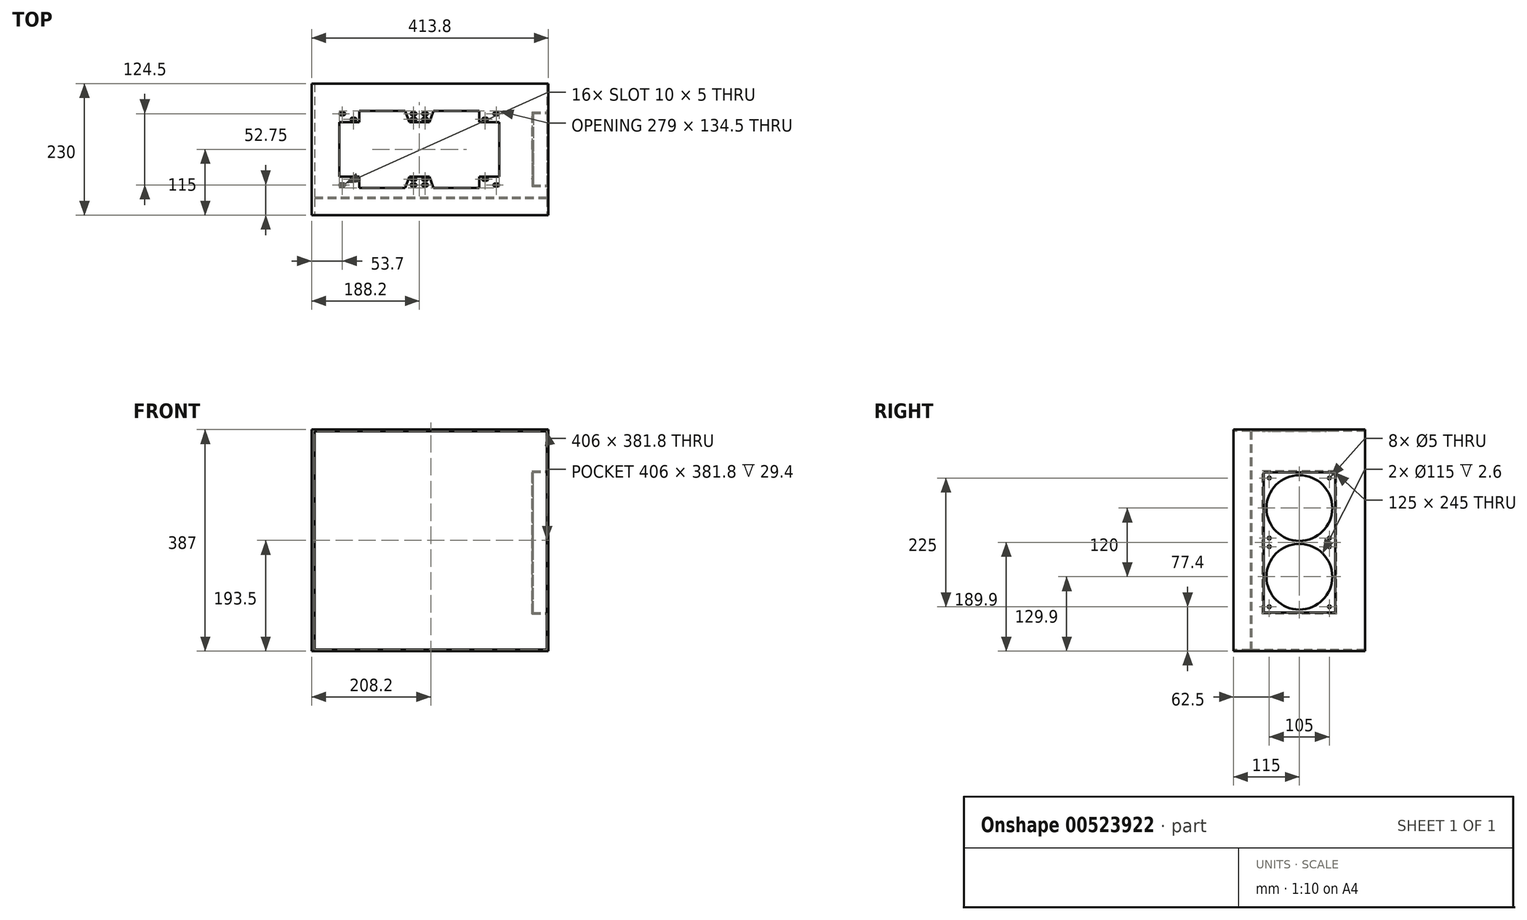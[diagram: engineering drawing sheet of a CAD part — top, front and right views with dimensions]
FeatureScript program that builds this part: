
annotation { "Feature Type Name" : "Feature", "Feature Type Description" : "" }
export const myFeature = defineFeature(function(context is Context, id is Id, definition is map)
    precondition{}
    {
        {
            var Q0;
            Q0=qCreatedBy(makeId("Front.planeOp"),FACE);
            var sketch = newSketch(context, id + "F0", { "sketchPlane" : qUnion([Q0])});
            skLineSegment(sketch, "E0.bottom", {"start": v(0, 0) * mm, "end": v(424, 0) * mm});
            skLineSegment(sketch, "E0.top", {"start": v(0, 397) * mm, "end": v(424, 397) * mm});
            skLineSegment(sketch, "E0.left", {"start": v(0, 0) * mm, "end": v(0, 397) * mm});
            skLineSegment(sketch, "E0.right", {"start": v(424, 0) * mm, "end": v(424, 397) * mm});
            skSolve(sketch);
        }
        {
            var Q0;
            Q0=makeQuery(id+"F0.imprint","IMPRINT",FACE,{"disambiguationData":[TD([[makeQuery(id+"F0.imprint","IMPRINT",EDGE,{"derivedFrom":sQuery(id+"F0.wireOp",EDGE,"E0.bottom")}),1.0]])]});
            extrude(context, id + "F1", {"entities" : qUnion([Q0]), "depth" : 230 * mm});
        }
        {
            var Q0;
            Q0=makeQuery(id+"F1.opExtrude","CAP_FACE",FACE,{"disambiguationData":[OSD([sQuery(id+"F0.wireOp",EDGE,"E0.bottom"),sQuery(id+"F0.wireOp",EDGE,"E0.top"),sQuery(id+"F0.wireOp",EDGE,"E0.left"),sQuery(id+"F0.wireOp",EDGE,"E0.right")])],"isStart":false});
            var sketch = newSketch(context, id + "F2", { "sketchPlane" : qUnion([Q0])});
            skLineSegment(sketch, "E1.bottom", {"start": v(5.2, 2.6) * mm, "end": v(411.2, 2.6) * mm});
            skLineSegment(sketch, "E1.top", {"start": v(5.2, 384.4) * mm, "end": v(411.2, 384.4) * mm});
            skLineSegment(sketch, "E1.left", {"start": v(5.2, 2.6) * mm, "end": v(5.2, 384.4) * mm});
            skLineSegment(sketch, "E1.right", {"start": v(411.2, 2.6) * mm, "end": v(411.2, 384.4) * mm});
            skSolve(sketch);
        }
        {
            var Q0;
            Q0=qSketchRegion(id+"F2",true);
            extrude(context, id + "F3", {"entities" : qUnion([Q0]), "operationType" : NewBodyOperationType.REMOVE, "endBound" : BoundingType.THROUGH_ALL, "oppositeDirection" : true, "depth" : 198 * mm});
        }
        {
            var Q0;
            Q0=makeQuery(id+"F1.opExtrude","CAP_FACE",FACE,{"disambiguationData":[OSD([sQuery(id+"F0.wireOp",EDGE,"E0.bottom"),sQuery(id+"F0.wireOp",EDGE,"E0.top"),sQuery(id+"F0.wireOp",EDGE,"E0.left"),sQuery(id+"F0.wireOp",EDGE,"E0.right")])],"isStart":false});
            var sketch = newSketch(context, id + "F4", { "sketchPlane" : qUnion([Q0])});
            skLineSegment(sketch, "E2.bottom", {"start": v(0, 397) * mm, "end": v(424, 397) * mm});
            skLineSegment(sketch, "E2.top", {"start": v(0, 387) * mm, "end": v(413.8, 387) * mm});
            skLineSegment(sketch, "E2.left", {"start": v(0, 397) * mm, "end": v(0, 387) * mm});
            skLineSegment(sketch, "E3.bottom", {"start": v(424, 0) * mm, "end": v(413.8, 0) * mm});
            skLineSegment(sketch, "E3.left", {"start": v(424, 0) * mm, "end": v(424, 397) * mm});
            skLineSegment(sketch, "E3.right", {"start": v(413.8, 0) * mm, "end": v(413.8, 387) * mm});
            skSolve(sketch);
        }
        {
            var Q0;
            Q0=qSketchRegion(id+"F4",true);
            extrude(context, id + "F5", {"entities" : qUnion([Q0]), "operationType" : NewBodyOperationType.REMOVE, "endBound" : BoundingType.THROUGH_ALL, "oppositeDirection" : true, "depth" : 25 * mm});
        }
        {
            var Q0;
            Q0=makeQuery(id+"F5.boolean.opBoolean","COPY",FACE,{"derivedFrom":makeQuery(id+"F5.opExtrude","SWEPT_FACE",FACE,{"disambiguationData":[OSD([sQuery(id+"F4.wireOp",EDGE,"E2.top")])]})});
            var sketch = newSketch(context, id + "F6", { "sketchPlane" : qUnion([Q0])});
            skLineSegment(sketch, "E4", {"start": v(413.8, -115) * mm, "end": v(0, -115) * mm, "construction": true});
            skPoint(sketch, "E5", {"position": v(303.2, -62.5) * mm});
            skPoint(sketch, "E6", {"position": v(303.2, -167.5) * mm});
            skPoint(sketch, "E7", {"position": v(322.7, -52.75) * mm});
            skPoint(sketch, "E8", {"position": v(322.7, -177.25) * mm});
            skPoint(sketch, "E9", {"position": v(198.2, -62.5) * mm});
            skPoint(sketch, "E10", {"position": v(198.2, -52.75) * mm});
            skPoint(sketch, "E11", {"position": v(198.2, -167.5) * mm});
            skPoint(sketch, "E12", {"position": v(198.2, -177.25) * mm});
            skPoint(sketch, "E13", {"position": v(178.2, -52.75) * mm});
            skPoint(sketch, "E14", {"position": v(178.2, -62.5) * mm});
            skPoint(sketch, "E15", {"position": v(178.2, -167.5) * mm});
            skPoint(sketch, "E16", {"position": v(178.2, -177.25) * mm});
            skPoint(sketch, "E17", {"position": v(73.2, -62.5) * mm});
            skPoint(sketch, "E18", {"position": v(73.2, -167.5) * mm});
            skPoint(sketch, "E19", {"position": v(53.7, -52.75) * mm});
            skPoint(sketch, "E20", {"position": v(53.7, -177.25) * mm});
            skLineSegment(sketch, "E21", {"start": v(48.7, -115) * mm, "end": v(48.7, -67.5) * mm});
            skLineSegment(sketch, "E22", {"start": v(48.7, -67.5) * mm, "end": v(83.2, -67.5) * mm});
            skLineSegment(sketch, "E23", {"start": v(83.2, -67.5) * mm, "end": v(83.2, -47.75) * mm});
            skLineSegment(sketch, "E24", {"start": v(83.2, -47.75) * mm, "end": v(163.2, -47.75) * mm});
            skLineSegment(sketch, "E25", {"start": v(163.2, -47.75) * mm, "end": v(170.7, -67.5) * mm});
            skLineSegment(sketch, "E26", {"start": v(170.7, -67.5) * mm, "end": v(205.7, -67.5) * mm});
            skLineSegment(sketch, "E27", {"start": v(205.7, -67.5) * mm, "end": v(213.2, -47.75) * mm});
            skLineSegment(sketch, "E28", {"start": v(213.2, -47.75) * mm, "end": v(293.2, -47.75) * mm});
            skLineSegment(sketch, "E29", {"start": v(293.2, -47.75) * mm, "end": v(293.2, -67.5) * mm});
            skLineSegment(sketch, "E30", {"start": v(293.2, -67.5) * mm, "end": v(327.7, -67.5) * mm});
            skLineSegment(sketch, "E31", {"start": v(327.7, -67.5) * mm, "end": v(327.7, -115) * mm});
            skLineSegment(sketch, "E32", {"start": v(178.2, -62.5) * mm, "end": v(198.2, -62.5) * mm, "construction": true});
            skPoint(sketch, "E33", {"position": v(188.2, -67.5) * mm});
            skPoint(sketch, "E34", {"position": v(188.2, -62.5) * mm});
            skLineSegment(sketch, "E35.MirrorCS", {"start": v(327.7, -162.5) * mm, "end": v(327.7, -115) * mm});
            skLineSegment(sketch, "E36.MirrorCS", {"start": v(293.2, -162.5) * mm, "end": v(327.7, -162.5) * mm});
            skLineSegment(sketch, "E37.MirrorCS", {"start": v(293.2, -182.25) * mm, "end": v(293.2, -162.5) * mm});
            skLineSegment(sketch, "E38.MirrorCS", {"start": v(213.2, -182.25) * mm, "end": v(293.2, -182.25) * mm});
            skLineSegment(sketch, "E39.MirrorCS", {"start": v(205.7, -162.5) * mm, "end": v(213.2, -182.25) * mm});
            skLineSegment(sketch, "E40.MirrorCS", {"start": v(170.7, -162.5) * mm, "end": v(205.7, -162.5) * mm});
            skLineSegment(sketch, "E41.MirrorCS", {"start": v(163.2, -182.25) * mm, "end": v(170.7, -162.5) * mm});
            skLineSegment(sketch, "E42.MirrorCS", {"start": v(83.2, -182.25) * mm, "end": v(163.2, -182.25) * mm});
            skLineSegment(sketch, "E43.MirrorCS", {"start": v(83.2, -162.5) * mm, "end": v(83.2, -182.25) * mm});
            skLineSegment(sketch, "E44.MirrorCS", {"start": v(48.7, -115) * mm, "end": v(48.7, -162.5) * mm});
            skLineSegment(sketch, "E45.MirrorCS", {"start": v(48.7, -162.5) * mm, "end": v(83.2, -162.5) * mm});
            skLineSegment(sketch, "E46.bottom", {"start": v(58.7, -50.25) * mm, "end": v(48.7, -50.25) * mm});
            skLineSegment(sketch, "E46.top", {"start": v(58.7, -55.25) * mm, "end": v(48.7, -55.25) * mm});
            skLineSegment(sketch, "E46.left", {"start": v(58.7, -50.25) * mm, "end": v(58.7, -55.25) * mm});
            skLineSegment(sketch, "E46.right", {"start": v(48.7, -50.25) * mm, "end": v(48.7, -55.25) * mm});
            skLineSegment(sketch, "E47.bottom", {"start": v(68.2, -60) * mm, "end": v(78.2, -60) * mm});
            skLineSegment(sketch, "E47.top", {"start": v(68.2, -65) * mm, "end": v(78.2, -65) * mm});
            skLineSegment(sketch, "E47.left", {"start": v(68.2, -60) * mm, "end": v(68.2, -65) * mm});
            skLineSegment(sketch, "E47.right", {"start": v(78.2, -60) * mm, "end": v(78.2, -65) * mm});
            skLineSegment(sketch, "E48.bottom", {"start": v(173.2, -50.25) * mm, "end": v(183.2, -50.25) * mm});
            skLineSegment(sketch, "E48.top", {"start": v(173.2, -55.25) * mm, "end": v(183.2, -55.25) * mm});
            skLineSegment(sketch, "E48.left", {"start": v(173.2, -50.25) * mm, "end": v(173.2, -55.25) * mm});
            skLineSegment(sketch, "E48.right", {"start": v(183.2, -50.25) * mm, "end": v(183.2, -55.25) * mm});
            skLineSegment(sketch, "E49.bottom", {"start": v(183.2, -60) * mm, "end": v(173.2, -60) * mm});
            skLineSegment(sketch, "E49.top", {"start": v(183.2, -65) * mm, "end": v(173.2, -65) * mm});
            skLineSegment(sketch, "E49.left", {"start": v(183.2, -60) * mm, "end": v(183.2, -65) * mm});
            skLineSegment(sketch, "E49.right", {"start": v(173.2, -60) * mm, "end": v(173.2, -65) * mm});
            skLineSegment(sketch, "E50.bottom", {"start": v(193.2, -50.25) * mm, "end": v(203.2, -50.25) * mm});
            skLineSegment(sketch, "E50.top", {"start": v(193.2, -55.25) * mm, "end": v(203.2, -55.25) * mm});
            skLineSegment(sketch, "E50.left", {"start": v(193.2, -50.25) * mm, "end": v(193.2, -55.25) * mm});
            skLineSegment(sketch, "E50.right", {"start": v(203.2, -50.25) * mm, "end": v(203.2, -55.25) * mm});
            skLineSegment(sketch, "E51.bottom", {"start": v(203.2, -60) * mm, "end": v(193.2, -60) * mm});
            skLineSegment(sketch, "E51.top", {"start": v(203.2, -65) * mm, "end": v(193.2, -65) * mm});
            skLineSegment(sketch, "E51.left", {"start": v(203.2, -60) * mm, "end": v(203.2, -65) * mm});
            skLineSegment(sketch, "E51.right", {"start": v(193.2, -60) * mm, "end": v(193.2, -65) * mm});
            skLineSegment(sketch, "E52.bottom", {"start": v(317.7, -50.25) * mm, "end": v(327.7, -50.25) * mm});
            skLineSegment(sketch, "E52.top", {"start": v(317.7, -55.25) * mm, "end": v(327.7, -55.25) * mm});
            skLineSegment(sketch, "E52.left", {"start": v(317.7, -50.25) * mm, "end": v(317.7, -55.25) * mm});
            skLineSegment(sketch, "E52.right", {"start": v(327.7, -50.25) * mm, "end": v(327.7, -55.25) * mm});
            skLineSegment(sketch, "E53.bottom", {"start": v(308.2, -60) * mm, "end": v(298.2, -60) * mm});
            skLineSegment(sketch, "E53.top", {"start": v(308.2, -65) * mm, "end": v(298.2, -65) * mm});
            skLineSegment(sketch, "E53.left", {"start": v(308.2, -60) * mm, "end": v(308.2, -65) * mm});
            skLineSegment(sketch, "E53.right", {"start": v(298.2, -60) * mm, "end": v(298.2, -65) * mm});
            skLineSegment(sketch, "E54.MirrorCS", {"start": v(48.7, -179.75) * mm, "end": v(48.7, -174.75) * mm});
            skLineSegment(sketch, "E55.MirrorCS", {"start": v(68.2, -165) * mm, "end": v(78.2, -165) * mm});
            skLineSegment(sketch, "E56.MirrorCS", {"start": v(68.2, -170) * mm, "end": v(78.2, -170) * mm});
            skLineSegment(sketch, "E57.MirrorCS", {"start": v(68.2, -170) * mm, "end": v(68.2, -165) * mm});
            skLineSegment(sketch, "E58.MirrorCS", {"start": v(58.7, -179.75) * mm, "end": v(48.7, -179.75) * mm});
            skLineSegment(sketch, "E59.MirrorCS", {"start": v(58.7, -179.75) * mm, "end": v(58.7, -174.75) * mm});
            skLineSegment(sketch, "E60.MirrorCS", {"start": v(78.2, -170) * mm, "end": v(78.2, -165) * mm});
            skLineSegment(sketch, "E61.MirrorCS", {"start": v(58.7, -174.75) * mm, "end": v(48.7, -174.75) * mm});
            skLineSegment(sketch, "E62.MirrorCS", {"start": v(193.2, -174.75) * mm, "end": v(203.2, -174.75) * mm});
            skLineSegment(sketch, "E63.MirrorCS", {"start": v(193.2, -179.75) * mm, "end": v(203.2, -179.75) * mm});
            skPoint(sketch, "E64.MirrorP", {"position": v(188.2, -167.5) * mm});
            skLineSegment(sketch, "E65.MirrorCS", {"start": v(173.2, -174.75) * mm, "end": v(183.2, -174.75) * mm});
            skLineSegment(sketch, "E66.MirrorCS", {"start": v(173.2, -170) * mm, "end": v(173.2, -165) * mm});
            skLineSegment(sketch, "E67.MirrorCS", {"start": v(203.2, -170) * mm, "end": v(203.2, -165) * mm});
            skPoint(sketch, "E68.MirrorP", {"position": v(188.2, -162.5) * mm});
            skLineSegment(sketch, "E69.MirrorCS", {"start": v(173.2, -179.75) * mm, "end": v(173.2, -174.75) * mm});
            skLineSegment(sketch, "E70.MirrorCS", {"start": v(193.2, -179.75) * mm, "end": v(193.2, -174.75) * mm});
            skLineSegment(sketch, "E71.MirrorCS", {"start": v(183.2, -165) * mm, "end": v(173.2, -165) * mm});
            skLineSegment(sketch, "E72.MirrorCS", {"start": v(178.2, -167.5) * mm, "end": v(198.2, -167.5) * mm, "construction": true});
            skLineSegment(sketch, "E73.MirrorCS", {"start": v(203.2, -165) * mm, "end": v(193.2, -165) * mm});
            skLineSegment(sketch, "E74.MirrorCS", {"start": v(203.2, -170) * mm, "end": v(193.2, -170) * mm});
            skLineSegment(sketch, "E75.MirrorCS", {"start": v(183.2, -170) * mm, "end": v(183.2, -165) * mm});
            skLineSegment(sketch, "E76.MirrorCS", {"start": v(193.2, -170) * mm, "end": v(193.2, -165) * mm});
            skLineSegment(sketch, "E77.MirrorCS", {"start": v(183.2, -179.75) * mm, "end": v(183.2, -174.75) * mm});
            skLineSegment(sketch, "E78.MirrorCS", {"start": v(173.2, -179.75) * mm, "end": v(183.2, -179.75) * mm});
            skLineSegment(sketch, "E79.MirrorCS", {"start": v(203.2, -179.75) * mm, "end": v(203.2, -174.75) * mm});
            skLineSegment(sketch, "E80.MirrorCS", {"start": v(183.2, -170) * mm, "end": v(173.2, -170) * mm});
            skLineSegment(sketch, "E81.MirrorCS", {"start": v(327.7, -179.75) * mm, "end": v(327.7, -174.75) * mm});
            skLineSegment(sketch, "E82.MirrorCS", {"start": v(308.2, -170) * mm, "end": v(298.2, -170) * mm});
            skLineSegment(sketch, "E83.MirrorCS", {"start": v(317.7, -179.75) * mm, "end": v(327.7, -179.75) * mm});
            skLineSegment(sketch, "E84.MirrorCS", {"start": v(298.2, -170) * mm, "end": v(298.2, -165) * mm});
            skLineSegment(sketch, "E85.MirrorCS", {"start": v(308.2, -165) * mm, "end": v(298.2, -165) * mm});
            skLineSegment(sketch, "E86.MirrorCS", {"start": v(308.2, -170) * mm, "end": v(308.2, -165) * mm});
            skLineSegment(sketch, "E87.MirrorCS", {"start": v(317.7, -174.75) * mm, "end": v(327.7, -174.75) * mm});
            skLineSegment(sketch, "E88.MirrorCS", {"start": v(317.7, -179.75) * mm, "end": v(317.7, -174.75) * mm});
            skSolve(sketch);
        }
        {
            var Q0;
            Q0=qSketchRegion(id+"F6",true);
            extrude(context, id + "F7", {"entities" : qUnion([Q0]), "operationType" : NewBodyOperationType.REMOVE, "endBound" : BoundingType.UP_TO_NEXT, "oppositeDirection" : true, "depth" : 25 * mm});
        }
        {
            var Q0;
            Q0=makeQuery(id+"F5.boolean.opBoolean","COPY",FACE,{"derivedFrom":makeQuery(id+"F5.opExtrude","SWEPT_FACE",FACE,{"disambiguationData":[OSD([sQuery(id+"F4.wireOp",EDGE,"E3.right")])]})});
            var sketch = newSketch(context, id + "F8", { "sketchPlane" : qUnion([Q0])});
            skCircle(sketch, "E89", {"center": v(-167.5, 302.4) * mm, "radius": 2.5 * mm, "construction": true});
            skCircle(sketch, "E90", {"center": v(-62.5, 302.4) * mm, "radius": 2.5 * mm, "construction": true});
            skCircle(sketch, "E91", {"center": v(-167.5, 197.4) * mm, "radius": 2.5 * mm, "construction": true});
            skCircle(sketch, "E92", {"center": v(-62.5, 197.4) * mm, "radius": 2.5 * mm, "construction": true});
            skCircle(sketch, "E93", {"center": v(-167.5, 182.4) * mm, "radius": 2.5 * mm, "construction": true});
            skCircle(sketch, "E94", {"center": v(-62.5, 182.4) * mm, "radius": 2.5 * mm, "construction": true});
            skCircle(sketch, "E95", {"center": v(-167.5, 77.4) * mm, "radius": 2.5 * mm, "construction": true});
            skCircle(sketch, "E96", {"center": v(-62.5, 77.4) * mm, "radius": 2.5 * mm, "construction": true});
            skLineSegment(sketch, "E97", {"start": v(-115, 387) * mm, "end": v(-115, 0) * mm, "construction": true});
            skLineSegment(sketch, "E98.bottom", {"start": v(-177.5, 312.4) * mm, "end": v(-52.5, 312.4) * mm});
            skLineSegment(sketch, "E98.top", {"start": v(-177.5, 67.4) * mm, "end": v(-52.5, 67.4) * mm});
            skLineSegment(sketch, "E98.left", {"start": v(-177.5, 312.4) * mm, "end": v(-177.5, 67.4) * mm});
            skLineSegment(sketch, "E98.right", {"start": v(-52.5, 312.4) * mm, "end": v(-52.5, 67.4) * mm});
            skSolve(sketch);
        }
        {
            var Q0;
            Q0=qSketchRegion(id+"F8",true);
            extrude(context, id + "F9", {"entities" : qUnion([Q0]), "operationType" : NewBodyOperationType.REMOVE, "endBound" : BoundingType.UP_TO_NEXT, "oppositeDirection" : true, "depth" : 46.66 * mm});
        }
        {
            var Q0;
            Q0=makeQuery(id+"F3.boolean.opBoolean","COPY",FACE,{"derivedFrom":makeQuery(id+"F3.opExtrude","SWEPT_FACE",FACE,{"disambiguationData":[OSD([sQuery(id+"F2.wireOp",EDGE,"E1.right")])]})});
            var sketch = newSketch(context, id + "F10", { "sketchPlane" : qUnion([Q0])});
            skLineSegment(sketch, "E99.bottom", {"start": v(177.5, 312.4) * mm, "end": v(52.5, 312.4) * mm});
            skLineSegment(sketch, "E99.top", {"start": v(177.5, 67.4) * mm, "end": v(52.5, 67.4) * mm});
            skLineSegment(sketch, "E99.left", {"start": v(177.5, 312.4) * mm, "end": v(177.5, 67.4) * mm});
            skLineSegment(sketch, "E99.right", {"start": v(52.5, 312.4) * mm, "end": v(52.5, 67.4) * mm});
            skLineSegment(sketch, "E100.bottom", {"start": v(49.9, 64.8) * mm, "end": v(180.1, 64.8) * mm});
            skLineSegment(sketch, "E100.top", {"start": v(49.9, 315) * mm, "end": v(180.1, 315) * mm});
            skLineSegment(sketch, "E100.left", {"start": v(49.9, 64.8) * mm, "end": v(49.9, 315) * mm});
            skLineSegment(sketch, "E100.right", {"start": v(180.1, 64.8) * mm, "end": v(180.1, 315) * mm});
            skSolve(sketch);
        }
        {
            var Q0;
            Q0=qSketchRegion(id+"F10",true);
            extrude(context, id + "F11", {"entities" : qUnion([Q0]), "operationType" : NewBodyOperationType.ADD, "depth" : 26 * mm});
        }
        {
            var Q0;
            Q0=makeQuery(id+"F11.opExtrude","CAP_FACE",FACE,{"disambiguationData":[OSD([sQuery(id+"F10.wireOp",EDGE,"E99.bottom"),sQuery(id+"F10.wireOp",EDGE,"E99.top"),sQuery(id+"F10.wireOp",EDGE,"E99.left"),sQuery(id+"F10.wireOp",EDGE,"E99.right"),sQuery(id+"F10.wireOp",EDGE,"E100.bottom"),sQuery(id+"F10.wireOp",EDGE,"E100.top"),sQuery(id+"F10.wireOp",EDGE,"E100.left"),sQuery(id+"F10.wireOp",EDGE,"E100.right")])],"isStart":false});
            var sketch = newSketch(context, id + "F12", { "sketchPlane" : qUnion([Q0])});
            skLineSegment(sketch, "E101.bottom", {"start": v(177.5, 67.4) * mm, "end": v(52.5, 67.4) * mm});
            skLineSegment(sketch, "E101.top", {"start": v(177.5, 312.4) * mm, "end": v(52.5, 312.4) * mm});
            skLineSegment(sketch, "E101.left", {"start": v(177.5, 67.4) * mm, "end": v(177.5, 312.4) * mm});
            skLineSegment(sketch, "E101.right", {"start": v(52.5, 67.4) * mm, "end": v(52.5, 312.4) * mm});
            skSolve(sketch);
        }
        {
            var Q0;
            Q0=qSketchRegion(id+"F12",true);
            extrude(context, id + "F13", {"entities" : qUnion([Q0]), "oppositeDirection" : true, "depth" : 2.6 * mm});
        }
        {
            var Q0;
            Q0=makeQuery(id+"F13.opExtrude","CAP_FACE",FACE,{"disambiguationData":[OSD([sQuery(id+"F12.wireOp",EDGE,"E101.bottom"),sQuery(id+"F12.wireOp",EDGE,"E101.top"),sQuery(id+"F12.wireOp",EDGE,"E101.left"),sQuery(id+"F12.wireOp",EDGE,"E101.right")])],"isStart":false});
            var sketch = newSketch(context, id + "F14", { "sketchPlane" : qUnion([Q0])});
            skCircle(sketch, "E102", {"center": v(-167.5, 302.4) * mm, "radius": 2.5 * mm});
            skCircle(sketch, "E103", {"center": v(-62.5, 302.4) * mm, "radius": 2.5 * mm});
            skCircle(sketch, "E104", {"center": v(-167.5, 197.4) * mm, "radius": 2.5 * mm});
            skCircle(sketch, "E105", {"center": v(-62.5, 197.4) * mm, "radius": 2.5 * mm});
            skCircle(sketch, "E106", {"center": v(-167.5, 182.4) * mm, "radius": 2.5 * mm});
            skCircle(sketch, "E107", {"center": v(-62.5, 182.4) * mm, "radius": 2.5 * mm});
            skCircle(sketch, "E108", {"center": v(-167.5, 77.4) * mm, "radius": 2.5 * mm});
            skCircle(sketch, "E109", {"center": v(-62.5, 77.4) * mm, "radius": 2.5 * mm});
            skLineSegment(sketch, "E110", {"start": v(-115, 312.4) * mm, "end": v(-115, 67.4) * mm, "construction": true});
            skLineSegment(sketch, "E111.bottom", {"start": v(-177.5, 312.4) * mm, "end": v(-52.5, 312.4) * mm, "construction": true});
            skLineSegment(sketch, "E111.top", {"start": v(-177.5, 67.4) * mm, "end": v(-52.5, 67.4) * mm, "construction": true});
            skLineSegment(sketch, "E111.left", {"start": v(-177.5, 312.4) * mm, "end": v(-177.5, 67.4) * mm, "construction": true});
            skLineSegment(sketch, "E111.right", {"start": v(-52.5, 312.4) * mm, "end": v(-52.5, 67.4) * mm, "construction": true});
            skCircle(sketch, "E112", {"center": v(-115, 249.9) * mm, "radius": 57.5 * mm});
            skCircle(sketch, "E113", {"center": v(-115, 129.9) * mm, "radius": 57.5 * mm});
            skSolve(sketch);
        }
        {
            var Q0;
            Q0=qSketchRegion(id+"F14",true);
            extrude(context, id + "F15", {"entities" : qUnion([Q0]), "operationType" : NewBodyOperationType.REMOVE, "endBound" : BoundingType.UP_TO_NEXT, "oppositeDirection" : true, "depth" : 25 * mm});
        }
        {
            var Q0;
            Q0=makeQuery(id+"F7.boolean.opBoolean","COPY",EDGE,{"derivedFrom":makeQuery(id+"F7.opExtrude","SWEPT_EDGE",EDGE,{"disambiguationData":[OSD([sQuery(id+"F6.wireOp",EDGE,"E46.bottom"),sQuery(id+"F6.wireOp",EDGE,"E46.right")])]})});
            var Q1;
            Q1=makeQuery(id+"F7.boolean.opBoolean","COPY",EDGE,{"derivedFrom":makeQuery(id+"F7.opExtrude","SWEPT_EDGE",EDGE,{"disambiguationData":[OSD([sQuery(id+"F6.wireOp",EDGE,"E46.bottom"),sQuery(id+"F6.wireOp",EDGE,"E46.left")])]})});
            var Q2;
            Q2=makeQuery(id+"F7.boolean.opBoolean","COPY",EDGE,{"derivedFrom":makeQuery(id+"F7.opExtrude","SWEPT_EDGE",EDGE,{"disambiguationData":[OSD([sQuery(id+"F6.wireOp",EDGE,"E46.top"),sQuery(id+"F6.wireOp",EDGE,"E46.left")])]})});
            var Q3;
            Q3=makeQuery(id+"F7.boolean.opBoolean","COPY",EDGE,{"derivedFrom":makeQuery(id+"F7.opExtrude","SWEPT_EDGE",EDGE,{"disambiguationData":[OSD([sQuery(id+"F6.wireOp",EDGE,"E46.top"),sQuery(id+"F6.wireOp",EDGE,"E46.right")])]})});
            var Q4;
            Q4=makeQuery(id+"F7.boolean.opBoolean","COPY",EDGE,{"derivedFrom":makeQuery(id+"F7.opExtrude","SWEPT_EDGE",EDGE,{"disambiguationData":[OSD([sQuery(id+"F6.wireOp",EDGE,"E47.bottom"),sQuery(id+"F6.wireOp",EDGE,"E47.left")])]})});
            var Q5;
            Q5=makeQuery(id+"F7.boolean.opBoolean","COPY",EDGE,{"derivedFrom":makeQuery(id+"F7.opExtrude","SWEPT_EDGE",EDGE,{"disambiguationData":[OSD([sQuery(id+"F6.wireOp",EDGE,"E47.top"),sQuery(id+"F6.wireOp",EDGE,"E47.left")])]})});
            var Q6;
            Q6=makeQuery(id+"F7.boolean.opBoolean","COPY",EDGE,{"derivedFrom":makeQuery(id+"F7.opExtrude","SWEPT_EDGE",EDGE,{"disambiguationData":[OSD([sQuery(id+"F6.wireOp",EDGE,"E47.top"),sQuery(id+"F6.wireOp",EDGE,"E47.right")])]})});
            var Q7;
            Q7=makeQuery(id+"F7.boolean.opBoolean","COPY",EDGE,{"derivedFrom":makeQuery(id+"F7.opExtrude","SWEPT_EDGE",EDGE,{"disambiguationData":[OSD([sQuery(id+"F6.wireOp",EDGE,"E47.bottom"),sQuery(id+"F6.wireOp",EDGE,"E47.right")])]})});
            var Q8;
            Q8=makeQuery(id+"F7.boolean.opBoolean","COPY",EDGE,{"derivedFrom":makeQuery(id+"F7.opExtrude","SWEPT_EDGE",EDGE,{"disambiguationData":[OSD([sQuery(id+"F6.wireOp",EDGE,"E51.top"),sQuery(id+"F6.wireOp",EDGE,"E51.left")])]})});
            var Q9;
            Q9=makeQuery(id+"F7.boolean.opBoolean","COPY",EDGE,{"derivedFrom":makeQuery(id+"F7.opExtrude","SWEPT_EDGE",EDGE,{"disambiguationData":[OSD([sQuery(id+"F6.wireOp",EDGE,"E51.top"),sQuery(id+"F6.wireOp",EDGE,"E51.right")])]})});
            var Q10;
            Q10=makeQuery(id+"F7.boolean.opBoolean","COPY",EDGE,{"derivedFrom":makeQuery(id+"F7.opExtrude","SWEPT_EDGE",EDGE,{"disambiguationData":[OSD([sQuery(id+"F6.wireOp",EDGE,"E51.bottom"),sQuery(id+"F6.wireOp",EDGE,"E51.right")])]})});
            var Q11;
            Q11=makeQuery(id+"F7.boolean.opBoolean","COPY",EDGE,{"derivedFrom":makeQuery(id+"F7.opExtrude","SWEPT_EDGE",EDGE,{"disambiguationData":[OSD([sQuery(id+"F6.wireOp",EDGE,"E51.bottom"),sQuery(id+"F6.wireOp",EDGE,"E51.left")])]})});
            var Q12;
            Q12=makeQuery(id+"F7.boolean.opBoolean","COPY",EDGE,{"derivedFrom":makeQuery(id+"F7.opExtrude","SWEPT_EDGE",EDGE,{"disambiguationData":[OSD([sQuery(id+"F6.wireOp",EDGE,"E50.top"),sQuery(id+"F6.wireOp",EDGE,"E50.right")])]})});
            var Q13;
            Q13=makeQuery(id+"F7.boolean.opBoolean","COPY",EDGE,{"derivedFrom":makeQuery(id+"F7.opExtrude","SWEPT_EDGE",EDGE,{"disambiguationData":[OSD([sQuery(id+"F6.wireOp",EDGE,"E50.top"),sQuery(id+"F6.wireOp",EDGE,"E50.left")])]})});
            var Q14;
            Q14=makeQuery(id+"F7.boolean.opBoolean","COPY",EDGE,{"derivedFrom":makeQuery(id+"F7.opExtrude","SWEPT_EDGE",EDGE,{"disambiguationData":[OSD([sQuery(id+"F6.wireOp",EDGE,"E50.bottom"),sQuery(id+"F6.wireOp",EDGE,"E50.left")])]})});
            var Q15;
            Q15=makeQuery(id+"F7.boolean.opBoolean","COPY",EDGE,{"derivedFrom":makeQuery(id+"F7.opExtrude","SWEPT_EDGE",EDGE,{"disambiguationData":[OSD([sQuery(id+"F6.wireOp",EDGE,"E50.bottom"),sQuery(id+"F6.wireOp",EDGE,"E50.right")])]})});
            var Q16;
            Q16=makeQuery(id+"F7.boolean.opBoolean","COPY",EDGE,{"derivedFrom":makeQuery(id+"F7.opExtrude","SWEPT_EDGE",EDGE,{"disambiguationData":[OSD([sQuery(id+"F6.wireOp",EDGE,"E48.bottom"),sQuery(id+"F6.wireOp",EDGE,"E48.right")])]})});
            var Q17;
            Q17=makeQuery(id+"F7.boolean.opBoolean","COPY",EDGE,{"derivedFrom":makeQuery(id+"F7.opExtrude","SWEPT_EDGE",EDGE,{"disambiguationData":[OSD([sQuery(id+"F6.wireOp",EDGE,"E48.bottom"),sQuery(id+"F6.wireOp",EDGE,"E48.left")])]})});
            var Q18;
            Q18=makeQuery(id+"F7.boolean.opBoolean","COPY",EDGE,{"derivedFrom":makeQuery(id+"F7.opExtrude","SWEPT_EDGE",EDGE,{"disambiguationData":[OSD([sQuery(id+"F6.wireOp",EDGE,"E48.top"),sQuery(id+"F6.wireOp",EDGE,"E48.left")])]})});
            var Q19;
            Q19=makeQuery(id+"F7.boolean.opBoolean","COPY",EDGE,{"derivedFrom":makeQuery(id+"F7.opExtrude","SWEPT_EDGE",EDGE,{"disambiguationData":[OSD([sQuery(id+"F6.wireOp",EDGE,"E48.top"),sQuery(id+"F6.wireOp",EDGE,"E48.right")])]})});
            var Q20;
            Q20=makeQuery(id+"F7.boolean.opBoolean","COPY",EDGE,{"derivedFrom":makeQuery(id+"F7.opExtrude","SWEPT_EDGE",EDGE,{"disambiguationData":[OSD([sQuery(id+"F6.wireOp",EDGE,"E49.bottom"),sQuery(id+"F6.wireOp",EDGE,"E49.left")])]})});
            var Q21;
            Q21=makeQuery(id+"F7.boolean.opBoolean","COPY",EDGE,{"derivedFrom":makeQuery(id+"F7.opExtrude","SWEPT_EDGE",EDGE,{"disambiguationData":[OSD([sQuery(id+"F6.wireOp",EDGE,"E49.bottom"),sQuery(id+"F6.wireOp",EDGE,"E49.right")])]})});
            var Q22;
            Q22=makeQuery(id+"F7.boolean.opBoolean","COPY",EDGE,{"derivedFrom":makeQuery(id+"F7.opExtrude","SWEPT_EDGE",EDGE,{"disambiguationData":[OSD([sQuery(id+"F6.wireOp",EDGE,"E49.top"),sQuery(id+"F6.wireOp",EDGE,"E49.right")])]})});
            var Q23;
            Q23=makeQuery(id+"F7.boolean.opBoolean","COPY",EDGE,{"derivedFrom":makeQuery(id+"F7.opExtrude","SWEPT_EDGE",EDGE,{"disambiguationData":[OSD([sQuery(id+"F6.wireOp",EDGE,"E49.top"),sQuery(id+"F6.wireOp",EDGE,"E49.left")])]})});
            var Q24;
            Q24=makeQuery(id+"F7.boolean.opBoolean","COPY",EDGE,{"derivedFrom":makeQuery(id+"F7.opExtrude","SWEPT_EDGE",EDGE,{"disambiguationData":[OSD([sQuery(id+"F6.wireOp",EDGE,"E53.bottom"),sQuery(id+"F6.wireOp",EDGE,"E53.right")])]})});
            var Q25;
            Q25=makeQuery(id+"F7.boolean.opBoolean","COPY",EDGE,{"derivedFrom":makeQuery(id+"F7.opExtrude","SWEPT_EDGE",EDGE,{"disambiguationData":[OSD([sQuery(id+"F6.wireOp",EDGE,"E53.top"),sQuery(id+"F6.wireOp",EDGE,"E53.right")])]})});
            var Q26;
            Q26=makeQuery(id+"F7.boolean.opBoolean","COPY",EDGE,{"derivedFrom":makeQuery(id+"F7.opExtrude","SWEPT_EDGE",EDGE,{"disambiguationData":[OSD([sQuery(id+"F6.wireOp",EDGE,"E53.top"),sQuery(id+"F6.wireOp",EDGE,"E53.left")])]})});
            var Q27;
            Q27=makeQuery(id+"F7.boolean.opBoolean","COPY",EDGE,{"derivedFrom":makeQuery(id+"F7.opExtrude","SWEPT_EDGE",EDGE,{"disambiguationData":[OSD([sQuery(id+"F6.wireOp",EDGE,"E53.bottom"),sQuery(id+"F6.wireOp",EDGE,"E53.left")])]})});
            var Q28;
            Q28=makeQuery(id+"F7.boolean.opBoolean","COPY",EDGE,{"derivedFrom":makeQuery(id+"F7.opExtrude","SWEPT_EDGE",EDGE,{"disambiguationData":[OSD([sQuery(id+"F6.wireOp",EDGE,"E52.top"),sQuery(id+"F6.wireOp",EDGE,"E52.left")])]})});
            var Q29;
            Q29=makeQuery(id+"F7.boolean.opBoolean","COPY",EDGE,{"derivedFrom":makeQuery(id+"F7.opExtrude","SWEPT_EDGE",EDGE,{"disambiguationData":[OSD([sQuery(id+"F6.wireOp",EDGE,"E52.bottom"),sQuery(id+"F6.wireOp",EDGE,"E52.left")])]})});
            var Q30;
            Q30=makeQuery(id+"F7.boolean.opBoolean","COPY",EDGE,{"derivedFrom":makeQuery(id+"F7.opExtrude","SWEPT_EDGE",EDGE,{"disambiguationData":[OSD([sQuery(id+"F6.wireOp",EDGE,"E52.bottom"),sQuery(id+"F6.wireOp",EDGE,"E52.right")])]})});
            var Q31;
            Q31=makeQuery(id+"F7.boolean.opBoolean","COPY",EDGE,{"derivedFrom":makeQuery(id+"F7.opExtrude","SWEPT_EDGE",EDGE,{"disambiguationData":[OSD([sQuery(id+"F6.wireOp",EDGE,"E52.top"),sQuery(id+"F6.wireOp",EDGE,"E52.right")])]})});
            var Q32;
            Q32=makeQuery(id+"F7.boolean.opBoolean","COPY",EDGE,{"derivedFrom":makeQuery(id+"F7.opExtrude","SWEPT_EDGE",EDGE,{"disambiguationData":[OSD([sQuery(id+"F6.wireOp",EDGE,"E81.MirrorCS"),sQuery(id+"F6.wireOp",EDGE,"E87.MirrorCS")])]})});
            var Q33;
            Q33=makeQuery(id+"F7.boolean.opBoolean","COPY",EDGE,{"derivedFrom":makeQuery(id+"F7.opExtrude","SWEPT_EDGE",EDGE,{"disambiguationData":[OSD([sQuery(id+"F6.wireOp",EDGE,"E81.MirrorCS"),sQuery(id+"F6.wireOp",EDGE,"E83.MirrorCS")])]})});
            var Q34;
            Q34=makeQuery(id+"F7.boolean.opBoolean","COPY",EDGE,{"derivedFrom":makeQuery(id+"F7.opExtrude","SWEPT_EDGE",EDGE,{"disambiguationData":[OSD([sQuery(id+"F6.wireOp",EDGE,"E83.MirrorCS"),sQuery(id+"F6.wireOp",EDGE,"E88.MirrorCS")])]})});
            var Q35;
            Q35=makeQuery(id+"F7.boolean.opBoolean","COPY",EDGE,{"derivedFrom":makeQuery(id+"F7.opExtrude","SWEPT_EDGE",EDGE,{"disambiguationData":[OSD([sQuery(id+"F6.wireOp",EDGE,"E87.MirrorCS"),sQuery(id+"F6.wireOp",EDGE,"E88.MirrorCS")])]})});
            var Q36;
            Q36=makeQuery(id+"F7.boolean.opBoolean","COPY",EDGE,{"derivedFrom":makeQuery(id+"F7.opExtrude","SWEPT_EDGE",EDGE,{"disambiguationData":[OSD([sQuery(id+"F6.wireOp",EDGE,"E82.MirrorCS"),sQuery(id+"F6.wireOp",EDGE,"E86.MirrorCS")])]})});
            var Q37;
            Q37=makeQuery(id+"F7.boolean.opBoolean","COPY",EDGE,{"derivedFrom":makeQuery(id+"F7.opExtrude","SWEPT_EDGE",EDGE,{"disambiguationData":[OSD([sQuery(id+"F6.wireOp",EDGE,"E85.MirrorCS"),sQuery(id+"F6.wireOp",EDGE,"E86.MirrorCS")])]})});
            var Q38;
            Q38=makeQuery(id+"F7.boolean.opBoolean","COPY",EDGE,{"derivedFrom":makeQuery(id+"F7.opExtrude","SWEPT_EDGE",EDGE,{"disambiguationData":[OSD([sQuery(id+"F6.wireOp",EDGE,"E84.MirrorCS"),sQuery(id+"F6.wireOp",EDGE,"E85.MirrorCS")])]})});
            var Q39;
            Q39=makeQuery(id+"F7.boolean.opBoolean","COPY",EDGE,{"derivedFrom":makeQuery(id+"F7.opExtrude","SWEPT_EDGE",EDGE,{"disambiguationData":[OSD([sQuery(id+"F6.wireOp",EDGE,"E82.MirrorCS"),sQuery(id+"F6.wireOp",EDGE,"E84.MirrorCS")])]})});
            var Q40;
            Q40=makeQuery(id+"F7.boolean.opBoolean","COPY",EDGE,{"derivedFrom":makeQuery(id+"F7.opExtrude","SWEPT_EDGE",EDGE,{"disambiguationData":[OSD([sQuery(id+"F6.wireOp",EDGE,"E67.MirrorCS"),sQuery(id+"F6.wireOp",EDGE,"E73.MirrorCS")])]})});
            var Q41;
            Q41=makeQuery(id+"F7.boolean.opBoolean","COPY",EDGE,{"derivedFrom":makeQuery(id+"F7.opExtrude","SWEPT_EDGE",EDGE,{"disambiguationData":[OSD([sQuery(id+"F6.wireOp",EDGE,"E73.MirrorCS"),sQuery(id+"F6.wireOp",EDGE,"E76.MirrorCS")])]})});
            var Q42;
            Q42=makeQuery(id+"F7.boolean.opBoolean","COPY",EDGE,{"derivedFrom":makeQuery(id+"F7.opExtrude","SWEPT_EDGE",EDGE,{"disambiguationData":[OSD([sQuery(id+"F6.wireOp",EDGE,"E74.MirrorCS"),sQuery(id+"F6.wireOp",EDGE,"E76.MirrorCS")])]})});
            var Q43;
            Q43=makeQuery(id+"F7.boolean.opBoolean","COPY",EDGE,{"derivedFrom":makeQuery(id+"F7.opExtrude","SWEPT_EDGE",EDGE,{"disambiguationData":[OSD([sQuery(id+"F6.wireOp",EDGE,"E67.MirrorCS"),sQuery(id+"F6.wireOp",EDGE,"E74.MirrorCS")])]})});
            var Q44;
            Q44=makeQuery(id+"F7.boolean.opBoolean","COPY",EDGE,{"derivedFrom":makeQuery(id+"F7.opExtrude","SWEPT_EDGE",EDGE,{"disambiguationData":[OSD([sQuery(id+"F6.wireOp",EDGE,"E62.MirrorCS"),sQuery(id+"F6.wireOp",EDGE,"E79.MirrorCS")])]})});
            var Q45;
            Q45=makeQuery(id+"F7.boolean.opBoolean","COPY",EDGE,{"derivedFrom":makeQuery(id+"F7.opExtrude","SWEPT_EDGE",EDGE,{"disambiguationData":[OSD([sQuery(id+"F6.wireOp",EDGE,"E62.MirrorCS"),sQuery(id+"F6.wireOp",EDGE,"E70.MirrorCS")])]})});
            var Q46;
            Q46=makeQuery(id+"F7.boolean.opBoolean","COPY",EDGE,{"derivedFrom":makeQuery(id+"F7.opExtrude","SWEPT_EDGE",EDGE,{"disambiguationData":[OSD([sQuery(id+"F6.wireOp",EDGE,"E63.MirrorCS"),sQuery(id+"F6.wireOp",EDGE,"E70.MirrorCS")])]})});
            var Q47;
            Q47=makeQuery(id+"F7.boolean.opBoolean","COPY",EDGE,{"derivedFrom":makeQuery(id+"F7.opExtrude","SWEPT_EDGE",EDGE,{"disambiguationData":[OSD([sQuery(id+"F6.wireOp",EDGE,"E63.MirrorCS"),sQuery(id+"F6.wireOp",EDGE,"E79.MirrorCS")])]})});
            var Q48;
            Q48=makeQuery(id+"F7.boolean.opBoolean","COPY",EDGE,{"derivedFrom":makeQuery(id+"F7.opExtrude","SWEPT_EDGE",EDGE,{"disambiguationData":[OSD([sQuery(id+"F6.wireOp",EDGE,"E77.MirrorCS"),sQuery(id+"F6.wireOp",EDGE,"E78.MirrorCS")])]})});
            var Q49;
            Q49=makeQuery(id+"F7.boolean.opBoolean","COPY",EDGE,{"derivedFrom":makeQuery(id+"F7.opExtrude","SWEPT_EDGE",EDGE,{"disambiguationData":[OSD([sQuery(id+"F6.wireOp",EDGE,"E65.MirrorCS"),sQuery(id+"F6.wireOp",EDGE,"E77.MirrorCS")])]})});
            var Q50;
            Q50=makeQuery(id+"F7.boolean.opBoolean","COPY",EDGE,{"derivedFrom":makeQuery(id+"F7.opExtrude","SWEPT_EDGE",EDGE,{"disambiguationData":[OSD([sQuery(id+"F6.wireOp",EDGE,"E65.MirrorCS"),sQuery(id+"F6.wireOp",EDGE,"E69.MirrorCS")])]})});
            var Q51;
            Q51=makeQuery(id+"F7.boolean.opBoolean","COPY",EDGE,{"derivedFrom":makeQuery(id+"F7.opExtrude","SWEPT_EDGE",EDGE,{"disambiguationData":[OSD([sQuery(id+"F6.wireOp",EDGE,"E69.MirrorCS"),sQuery(id+"F6.wireOp",EDGE,"E78.MirrorCS")])]})});
            var Q52;
            Q52=makeQuery(id+"F7.boolean.opBoolean","COPY",EDGE,{"derivedFrom":makeQuery(id+"F7.opExtrude","SWEPT_EDGE",EDGE,{"disambiguationData":[OSD([sQuery(id+"F6.wireOp",EDGE,"E66.MirrorCS"),sQuery(id+"F6.wireOp",EDGE,"E71.MirrorCS")])]})});
            var Q53;
            Q53=makeQuery(id+"F7.boolean.opBoolean","COPY",EDGE,{"derivedFrom":makeQuery(id+"F7.opExtrude","SWEPT_EDGE",EDGE,{"disambiguationData":[OSD([sQuery(id+"F6.wireOp",EDGE,"E66.MirrorCS"),sQuery(id+"F6.wireOp",EDGE,"E80.MirrorCS")])]})});
            var Q54;
            Q54=makeQuery(id+"F7.boolean.opBoolean","COPY",EDGE,{"derivedFrom":makeQuery(id+"F7.opExtrude","SWEPT_EDGE",EDGE,{"disambiguationData":[OSD([sQuery(id+"F6.wireOp",EDGE,"E75.MirrorCS"),sQuery(id+"F6.wireOp",EDGE,"E80.MirrorCS")])]})});
            var Q55;
            Q55=makeQuery(id+"F7.boolean.opBoolean","COPY",EDGE,{"derivedFrom":makeQuery(id+"F7.opExtrude","SWEPT_EDGE",EDGE,{"disambiguationData":[OSD([sQuery(id+"F6.wireOp",EDGE,"E71.MirrorCS"),sQuery(id+"F6.wireOp",EDGE,"E75.MirrorCS")])]})});
            var Q56;
            Q56=makeQuery(id+"F7.boolean.opBoolean","COPY",EDGE,{"derivedFrom":makeQuery(id+"F7.opExtrude","SWEPT_EDGE",EDGE,{"disambiguationData":[OSD([sQuery(id+"F6.wireOp",EDGE,"E55.MirrorCS"),sQuery(id+"F6.wireOp",EDGE,"E60.MirrorCS")])]})});
            var Q57;
            Q57=makeQuery(id+"F7.boolean.opBoolean","COPY",EDGE,{"derivedFrom":makeQuery(id+"F7.opExtrude","SWEPT_EDGE",EDGE,{"disambiguationData":[OSD([sQuery(id+"F6.wireOp",EDGE,"E56.MirrorCS"),sQuery(id+"F6.wireOp",EDGE,"E60.MirrorCS")])]})});
            var Q58;
            Q58=makeQuery(id+"F7.boolean.opBoolean","COPY",EDGE,{"derivedFrom":makeQuery(id+"F7.opExtrude","SWEPT_EDGE",EDGE,{"disambiguationData":[OSD([sQuery(id+"F6.wireOp",EDGE,"E56.MirrorCS"),sQuery(id+"F6.wireOp",EDGE,"E57.MirrorCS")])]})});
            var Q59;
            Q59=makeQuery(id+"F7.boolean.opBoolean","COPY",EDGE,{"derivedFrom":makeQuery(id+"F7.opExtrude","SWEPT_EDGE",EDGE,{"disambiguationData":[OSD([sQuery(id+"F6.wireOp",EDGE,"E55.MirrorCS"),sQuery(id+"F6.wireOp",EDGE,"E57.MirrorCS")])]})});
            var Q60;
            Q60=makeQuery(id+"F7.boolean.opBoolean","COPY",EDGE,{"derivedFrom":makeQuery(id+"F7.opExtrude","SWEPT_EDGE",EDGE,{"disambiguationData":[OSD([sQuery(id+"F6.wireOp",EDGE,"E54.MirrorCS"),sQuery(id+"F6.wireOp",EDGE,"E61.MirrorCS")])]})});
            var Q61;
            Q61=makeQuery(id+"F7.boolean.opBoolean","COPY",EDGE,{"derivedFrom":makeQuery(id+"F7.opExtrude","SWEPT_EDGE",EDGE,{"disambiguationData":[OSD([sQuery(id+"F6.wireOp",EDGE,"E54.MirrorCS"),sQuery(id+"F6.wireOp",EDGE,"E58.MirrorCS")])]})});
            var Q62;
            Q62=makeQuery(id+"F7.boolean.opBoolean","COPY",EDGE,{"derivedFrom":makeQuery(id+"F7.opExtrude","SWEPT_EDGE",EDGE,{"disambiguationData":[OSD([sQuery(id+"F6.wireOp",EDGE,"E58.MirrorCS"),sQuery(id+"F6.wireOp",EDGE,"E59.MirrorCS")])]})});
            var Q63;
            Q63=makeQuery(id+"F7.boolean.opBoolean","COPY",EDGE,{"derivedFrom":makeQuery(id+"F7.opExtrude","SWEPT_EDGE",EDGE,{"disambiguationData":[OSD([sQuery(id+"F6.wireOp",EDGE,"E59.MirrorCS"),sQuery(id+"F6.wireOp",EDGE,"E61.MirrorCS")])]})});
            fillet(context, id + "F16", {"entities" : qUnion([Q0, Q1, Q2, Q3, Q4, Q5, Q6, Q7, Q8, Q9, Q10, Q11, Q12, Q13, Q14, Q15, Q16, Q17, Q18, Q19, Q20, Q21, Q22, Q23, Q24, Q25, Q26, Q27, Q28, Q29, Q30, Q31, Q32, Q33, Q34, Q35, Q36, Q37, Q38, Q39, Q40, Q41, Q42, Q43, Q44, Q45, Q46, Q47, Q48, Q49, Q50, Q51, Q52, Q53, Q54, Q55, Q56, Q57, Q58, Q59, Q60, Q61, Q62, Q63]), "radius" : 2.5 * mm, "tangentPropagation" : true, "allowEdgeOverflow" : false});
        }
        {
            var Q0;
            Q0=makeQuery(id+"F1.opExtrude","CAP_FACE",FACE,{"disambiguationData":[OSD([sQuery(id+"F0.wireOp",EDGE,"E0.bottom"),sQuery(id+"F0.wireOp",EDGE,"E0.top"),sQuery(id+"F0.wireOp",EDGE,"E0.left"),sQuery(id+"F0.wireOp",EDGE,"E0.right")])],"isStart":false});
            cPlane(context, id + "F17", {"entities" : qUnion([Q0]), "cplaneType" : CPlaneType.OFFSET, "offset" : 198 * mm, "oppositeDirection" : true, "width" : 150 * mm, "height" : 150 * mm});
        }
        {
            var Q0;
            Q0=qCreatedBy(id+"F17.planeOp",FACE);
            var sketch = newSketch(context, id + "F18", { "sketchPlane" : qUnion([Q0])});
            skLineSegment(sketch, "E114.bottom", {"start": v(5.2, 384.4) * mm, "end": v(411.2, 384.4) * mm});
            skLineSegment(sketch, "E114.top", {"start": v(5.2, 2.6) * mm, "end": v(411.2, 2.6) * mm});
            skLineSegment(sketch, "E114.left", {"start": v(5.2, 384.4) * mm, "end": v(5.2, 2.6) * mm});
            skLineSegment(sketch, "E114.right", {"start": v(411.2, 384.4) * mm, "end": v(411.2, 2.6) * mm});
            skSolve(sketch);
        }
        {
            var Q0;
            Q0=makeQuery(id+"F1.opExtrude","CAP_FACE",FACE,{"disambiguationData":[OSD([sQuery(id+"F0.wireOp",EDGE,"E0.bottom"),sQuery(id+"F0.wireOp",EDGE,"E0.top"),sQuery(id+"F0.wireOp",EDGE,"E0.left"),sQuery(id+"F0.wireOp",EDGE,"E0.right")])],"isStart":false});
            cPlane(context, id + "F19", {"entities" : qUnion([Q0]), "cplaneType" : CPlaneType.OFFSET, "offset" : (230 - 198) * mm, "oppositeDirection" : true, "width" : 150 * mm, "height" : 150 * mm});
        }
        {
            var Q0;
            Q0=qCreatedBy(id+"F19.planeOp",FACE);
            var sketch = newSketch(context, id + "F20", { "sketchPlane" : qUnion([Q0])});
            skLineSegment(sketch, "E115.bottom", {"start": v(5.2, 384.4) * mm, "end": v(411.2, 384.4) * mm});
            skLineSegment(sketch, "E115.top", {"start": v(5.2, 2.6) * mm, "end": v(411.2, 2.6) * mm});
            skLineSegment(sketch, "E115.left", {"start": v(5.2, 384.4) * mm, "end": v(5.2, 2.6) * mm});
            skLineSegment(sketch, "E115.right", {"start": v(411.2, 384.4) * mm, "end": v(411.2, 2.6) * mm});
            skSolve(sketch);
        }
        {
            var Q0;
            Q0=qSketchRegion(id+"F20",true);
            extrude(context, id + "F21", {"entities" : qUnion([Q0]), "operationType" : NewBodyOperationType.ADD, "depth" : 2.6 * mm});
        }
    });
